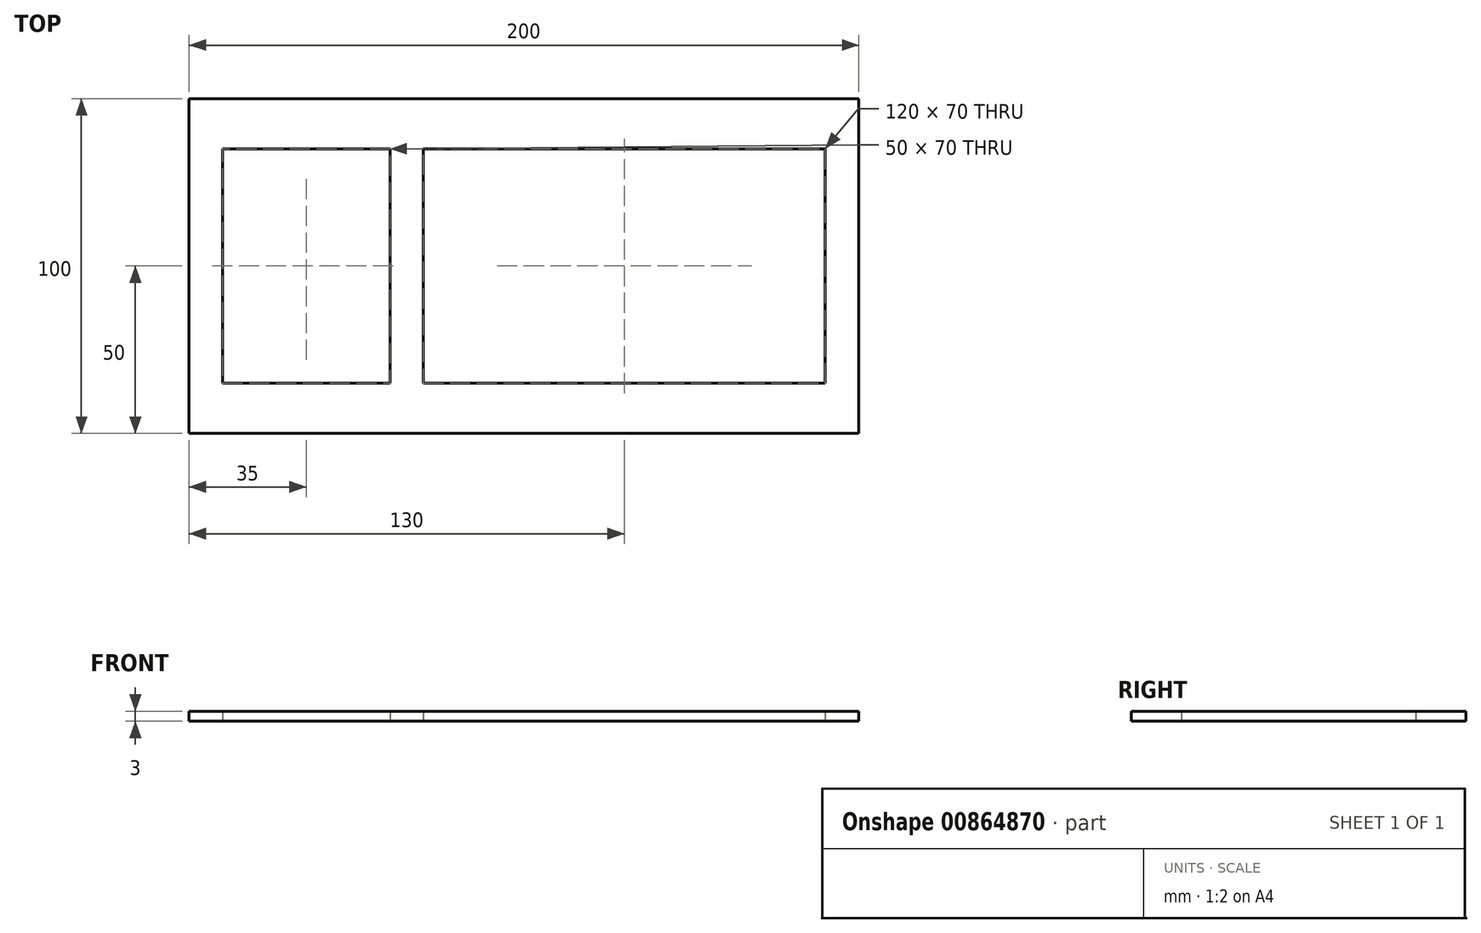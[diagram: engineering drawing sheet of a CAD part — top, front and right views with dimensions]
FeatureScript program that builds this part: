
annotation { "Feature Type Name" : "Feature", "Feature Type Description" : "" }
export const myFeature = defineFeature(function(context is Context, id is Id, definition is map)
    precondition{}
    {
        {
            var Q0;
            Q0=qCreatedBy(makeId("Top.planeOp"),FACE);
            var sketch = newSketch(context, id + "F0", { "sketchPlane" : qUnion([Q0])});
            skLineSegment(sketch, "E0.bottom", {"start": v(100, -50) * mm, "end": v(-100, -50) * mm});
            skLineSegment(sketch, "E0.top", {"start": v(100, 50) * mm, "end": v(-100, 50) * mm});
            skLineSegment(sketch, "E0.left", {"start": v(100, -50) * mm, "end": v(100, 50) * mm});
            skLineSegment(sketch, "E0.right", {"start": v(-100, -50) * mm, "end": v(-100, 50) * mm});
            skPoint(sketch, "E0.middle", {"position": v(0, 0) * mm});
            skLineSegment(sketch, "E1.bottom", {"start": v(90, 35) * mm, "end": v(-30, 35) * mm});
            skLineSegment(sketch, "E1.top", {"start": v(90, -35) * mm, "end": v(-30, -35) * mm});
            skLineSegment(sketch, "E1.left", {"start": v(90, 35) * mm, "end": v(90, -35) * mm});
            skLineSegment(sketch, "E1.right", {"start": v(-30, 35) * mm, "end": v(-30, -35) * mm});
            skPoint(sketch, "E1.middle", {"position": v(30, 0) * mm});
            skLineSegment(sketch, "E2.bottom", {"start": v(-40, 35) * mm, "end": v(-90, 35) * mm});
            skLineSegment(sketch, "E2.top", {"start": v(-40, -35) * mm, "end": v(-90, -35) * mm});
            skLineSegment(sketch, "E2.left", {"start": v(-40, 35) * mm, "end": v(-40, -35) * mm});
            skLineSegment(sketch, "E2.right", {"start": v(-90, 35) * mm, "end": v(-90, -35) * mm});
            skPoint(sketch, "E2.middle", {"position": v(-65, 0) * mm});
            skSolve(sketch);
        }
        {
            var Q0;
            Q0 = qSketchRegion(id + "F0", true);
            extrude(context, id + "F1", {"entities" : qUnion([Q0]), "depth" : 3 * mm, "offsetDistance" : 25 * mm});
        }
    });
